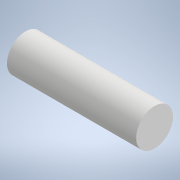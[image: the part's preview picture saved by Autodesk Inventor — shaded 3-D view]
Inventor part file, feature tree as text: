
AUTODESK INVENTOR PART (.ipt)
format: ipt  version: 2022.1 (Build 261234000, 234)  size: 96,256 bytes
history: native  units: mm
features: other x1, extrude x1, sketch x1
ambient origin geometry x8: Origin, YZ Plane, XZ Plane, XY Plane, X Axis, Y Axis, Z Axis, Center Point
bodies: Body1 (feature_tree)
feature tree (3):
  other  "Sólido1"
  extrude  "Extrusión1"  Depth=60.0mm TaperAngle=0.0deg
  sketch  "Boceto1"  dims[d0=20.0mm d1=60.0mm d2=0.0mm]
